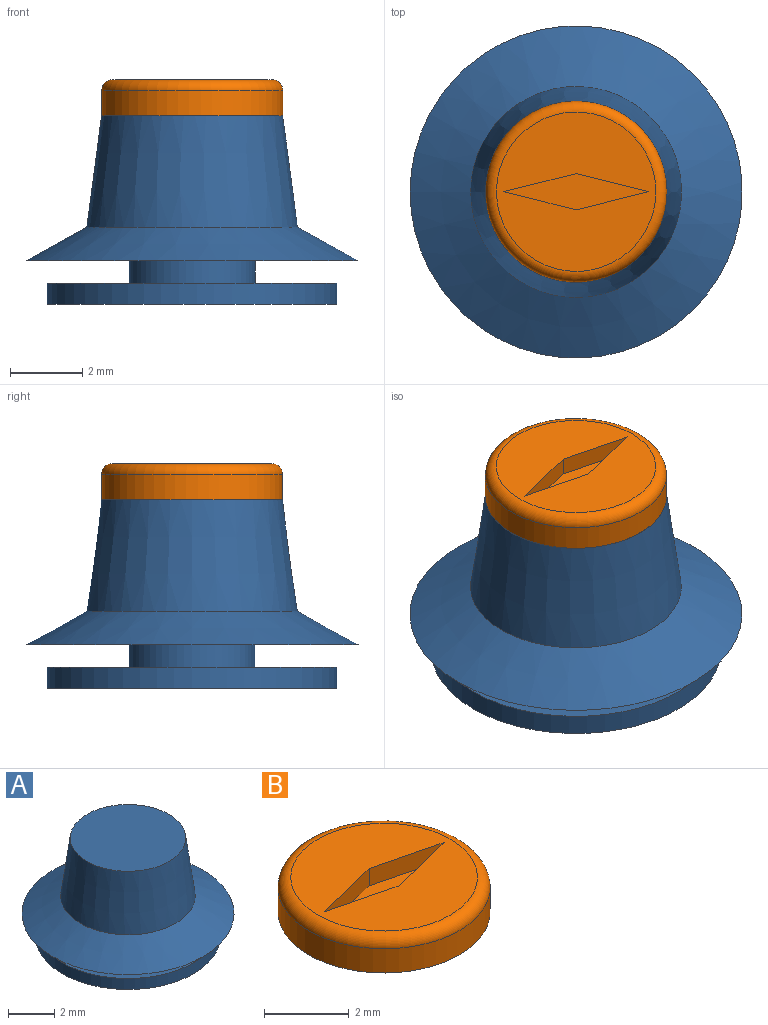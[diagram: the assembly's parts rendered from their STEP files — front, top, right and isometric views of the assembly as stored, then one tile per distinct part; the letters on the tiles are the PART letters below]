
ASSEMBLY  parts=2 mates=1
PART A: 8 faces, bbox 9.2x9.2x5.2 mm
  f0: plane 8x8mm, normal (0,0,-1), area 50.3mm2, adj f1
  f1: cylinder r=4mm len=8mm, axis (0,0,-1), area 14.6mm2, adj f0,f2
  f2: plane 8x8mm, normal (0,0,1), area 40.8mm2, adj f1,f3
  f3: cylinder r=1.74mm len=3.48mm, axis (0,0,-1), area 6.8mm2, adj f2,f4
  f4: plane 9.17x9.17mm, normal (0,0,-1), area 56.5mm2, adj f3,f5
  f5: cone r=2.91mm half-angle=61deg, axis (0,0,-1), area 45.1mm2, adj f4,f6
  f6: cone r=2.5mm half-angle=7.6deg, axis (0,0,-1), area 52.7mm2, adj f5,f7
  f7: plane 5x5mm, normal (0,0,1), area 19.6mm2, adj f6
PART B: 9 faces, bbox 5.4x5.4x1 mm
  f0: plane 4.4x4.4mm, normal (0,0,1), area 13.2mm2, adj f3,f4,f5,f6,f7
  f1: plane 5x5mm, normal (0,0,-1), area 19.6mm2, adj f2
  f2: cylinder r=2.5mm len=5mm, axis (0,0,1), area 11mm2, adj f1,f3
  f3: torus R=2.2mm, axis (0,0,1), area 7.1mm2, adj f0,f2
  f4: plane 2x0.5mm, normal (0.24,-0.97,0), area 1mm2, adj f0,f5,f7,f8
  f5: plane 2x0.5mm, normal (0.24,0.97,0), area 1mm2, adj f0,f4,f6,f8
  f6: plane 2x0.5mm, normal (-0.24,0.97,0), area 1mm2, adj f0,f5,f7,f8
  f7: plane 2x0.5mm, normal (-0.24,-0.97,0), area 1mm2, adj f0,f4,f6,f8
  f8: plane 4x1mm, normal (0,0,1), area 2mm2, adj f4,f5,f6,f7
PLACE A at identity fixed
PLACE B t=(0,0,5)mm
MATE fastened B.f2 <-> A.f1  axis (0,0,-1) through (0,0,4)mm
